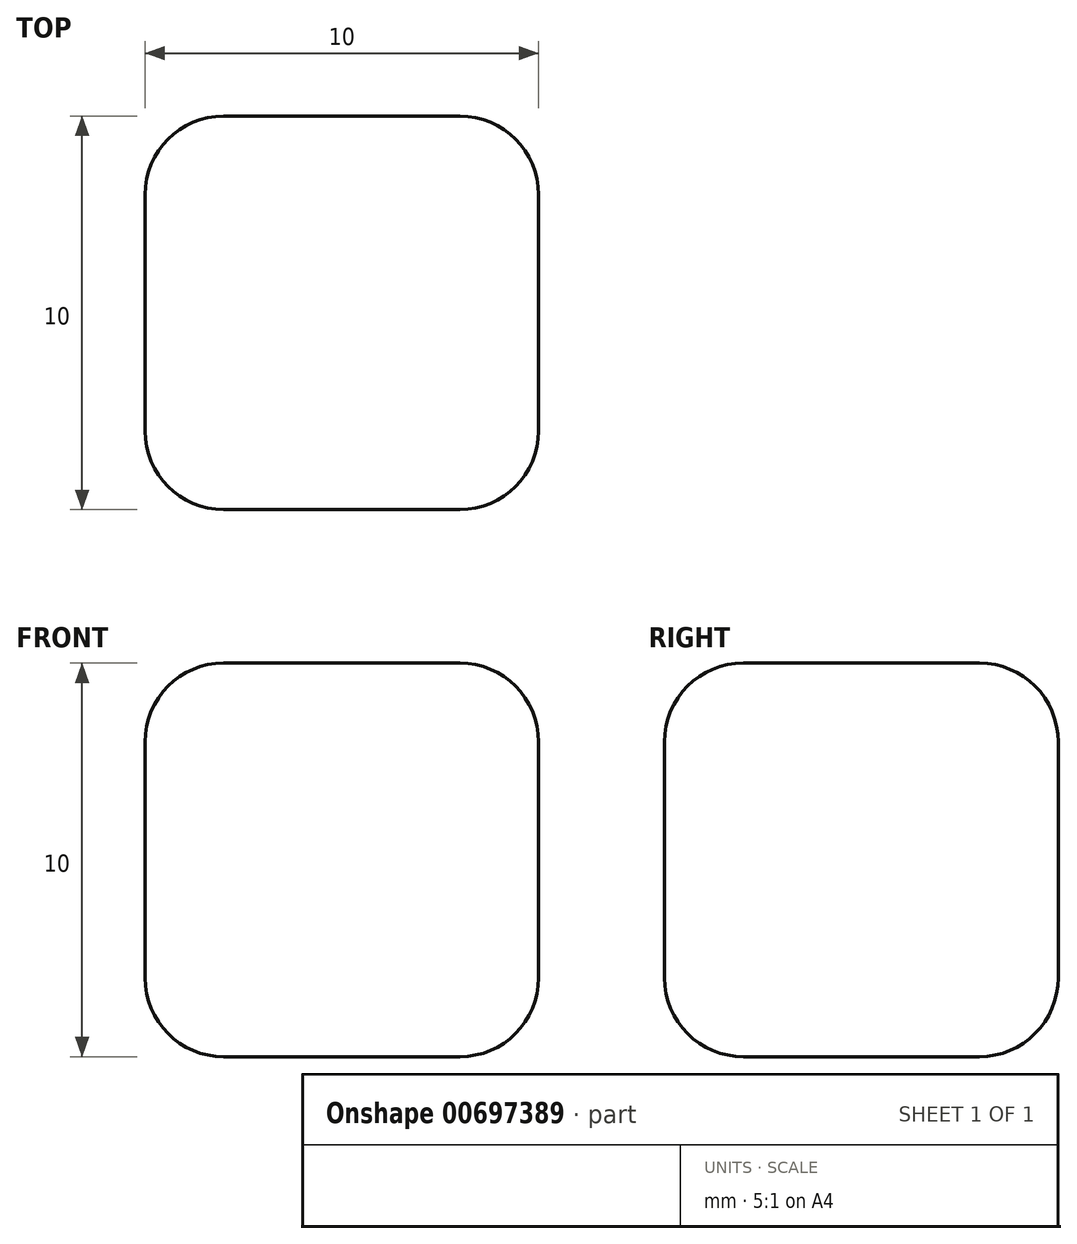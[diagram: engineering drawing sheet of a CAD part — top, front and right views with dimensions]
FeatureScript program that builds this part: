
annotation { "Feature Type Name" : "Feature", "Feature Type Description" : "" }
export const myFeature = defineFeature(function(context is Context, id is Id, definition is map)
    precondition{}
    {
        {
            var Q0;
            Q0=qCreatedBy(makeId("Top.planeOp"),FACE);
            var sketch = newSketch(context, id + "F0", { "sketchPlane" : qUnion([Q0])});
            skLineSegment(sketch, "E0.bottom", {"start": v(10, 10) * mm, "end": v(0, 10) * mm});
            skLineSegment(sketch, "E0.top", {"start": v(10, 0) * mm, "end": v(0, 0) * mm});
            skLineSegment(sketch, "E0.left", {"start": v(10, 10) * mm, "end": v(10, 0) * mm});
            skLineSegment(sketch, "E0.right", {"start": v(0, 10) * mm, "end": v(0, 0) * mm});
            skSolve(sketch);
        }
        {
            var Q0;
            Q0=makeQuery(id+"F0.imprint","IMPRINT",FACE,{"disambiguationData":[TD([[makeQuery(id+"F0.imprint","IMPRINT",EDGE,{"derivedFrom":sQuery(id+"F0.wireOp",EDGE,"E0.bottom")}),1.0]])]});
            extrude(context, id + "F1", {"entities" : qUnion([Q0]), "depth" : 10 * mm, "offsetDistance" : 25 * mm});
        }
        {
            var Q0;
            Q0=makeQuery(id+"F1.opExtrude","CAP_EDGE",EDGE,{"disambiguationData":[OSD([sQuery(id+"F0.wireOp",EDGE,"E0.left")])],"isStart":false});
            var Q1;
            Q1=makeQuery(id+"F1.opExtrude","CAP_EDGE",EDGE,{"disambiguationData":[OSD([sQuery(id+"F0.wireOp",EDGE,"E0.top")])],"isStart":false});
            var Q2;
            Q2=makeQuery(id+"F1.opExtrude","CAP_EDGE",EDGE,{"disambiguationData":[OSD([sQuery(id+"F0.wireOp",EDGE,"E0.right")])],"isStart":false});
            var Q3;
            Q3=makeQuery(id+"F1.opExtrude","CAP_EDGE",EDGE,{"disambiguationData":[OSD([sQuery(id+"F0.wireOp",EDGE,"E0.bottom")])],"isStart":false});
            var Q4;
            Q4=makeQuery(id+"F1.opExtrude","CAP_EDGE",EDGE,{"disambiguationData":[OSD([sQuery(id+"F0.wireOp",EDGE,"E0.left")])],"isStart":true});
            var Q5;
            Q5=makeQuery(id+"F1.opExtrude","SWEPT_EDGE",EDGE,{"disambiguationData":[OSD([sQuery(id+"F0.wireOp",EDGE,"E0.top"),sQuery(id+"F0.wireOp",EDGE,"E0.left")])]});
            var Q6;
            Q6=makeQuery(id+"F1.opExtrude","SWEPT_EDGE",EDGE,{"disambiguationData":[OSD([sQuery(id+"F0.wireOp",EDGE,"E0.top"),sQuery(id+"F0.wireOp",EDGE,"E0.right")])]});
            var Q7;
            Q7=makeQuery(id+"F1.opExtrude","SWEPT_EDGE",EDGE,{"disambiguationData":[OSD([sQuery(id+"F0.wireOp",EDGE,"E0.bottom"),sQuery(id+"F0.wireOp",EDGE,"E0.left")])]});
            var Q8;
            Q8=makeQuery(id+"F1.opExtrude","CAP_EDGE",EDGE,{"disambiguationData":[OSD([sQuery(id+"F0.wireOp",EDGE,"E0.top")])],"isStart":true});
            var Q9;
            Q9=makeQuery(id+"F1.opExtrude","CAP_EDGE",EDGE,{"disambiguationData":[OSD([sQuery(id+"F0.wireOp",EDGE,"E0.right")])],"isStart":true});
            var Q10;
            Q10=makeQuery(id+"F1.opExtrude","CAP_EDGE",EDGE,{"disambiguationData":[OSD([sQuery(id+"F0.wireOp",EDGE,"E0.bottom")])],"isStart":true});
            var Q11;
            Q11=makeQuery(id+"F1.opExtrude","SWEPT_EDGE",EDGE,{"disambiguationData":[OSD([sQuery(id+"F0.wireOp",EDGE,"E0.bottom"),sQuery(id+"F0.wireOp",EDGE,"E0.right")])]});
            fillet(context, id + "F2", {"entities" : qUnion([Q0, Q1, Q2, Q3, Q4, Q5, Q6, Q7, Q8, Q9, Q10, Q11]), "radius" : 2 * mm, "tangentPropagation" : true, "allowEdgeOverflow" : false});
        }
    });
